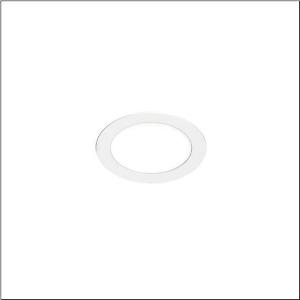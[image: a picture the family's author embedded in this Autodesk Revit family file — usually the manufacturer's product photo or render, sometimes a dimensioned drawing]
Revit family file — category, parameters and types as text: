
# Revit family: lunis_41_flat_51dr107dhba
name_source: partatom
category: Lighting Fixtures
units: mm (PartAtom-declared; Revit-internal decimal feet)

## family parameters
Cut with Voids When Loaded = No
Host = Face
Light Source = No
Part Type = Normal
Room Calculation Point = No
Round Connector Dimension = Use Diameter
Shared = No

## types (1)
- --- (1 x LED, 1360 lm, 15 W, 5700K)
    Apparent Load = 15 VA
    CIE Flux Codes = 49 80 96 100 100
    Color Rendering = 80
    Color Temperature = 5700K
    Default Elevation = 1800 mm
    Description = Lunis 41,  flat, downlight, light emission: direct distribution, LED rated luminous flux: 1.360lm, light colour: 840/857, control gear: ECG, mains connection: 230V, AC, 50/60Hz, housing, round, of aluminium, coated, traffic white (RAL 9016), diameter: 170mm, protection rating (complete): IP20, protection rating (on room side): IP44, insulation class (complete): insulation class II (safety insulation), certification: CE, permissible ambient temperature for indoor applications: -20..+40°C, packaging unit: 1 piece
    Height = 0 mm  [stored 0 ft]
    Lamp = 1 x LED
    Lamp Light Flux = 1360 lm
    Lamp Power = 15 W
    Lamp count = 1
    Length = 170 mm  [stored 0.557743 ft]
    Luminous efficacy = 91 lm/W
    Manufacturer = Siteco
    ModVariant = No
    Model = 51DR107DHBA
    Mounting Place = Ceiling
    Mounting Type = Recessed
    Number of Poles = 1
    OnlyDefault = Yes
    Power Factor = 1
    Product Name = Lunis 41 flat
    Product group = downlight
    ProductGroupID = 400
    Protection Class = Protection class II
    Protection Degree = IP 20
    RLX_Detail_Level = 1
    RLX_Emergency_Light_Flux = 0 lm
    RLX_Emergency_Type = 0
    RLX_Emergency_Type_DB = No
    RlxData = <blob elided: 24273 chars, md5=9e7785de>
    Socket = socket
    Standby Power = 0 W
    System Light Flux = 1360 lm
    System Power = 15 W
    Type Comments = factory setting: colour temperature 5700K
    Type Image = l_1007045.jpg
    URL = http://relux.com
    VarID = @adj_130679
    Voltage = 0 V
    Weight = 0.00 kg
    Width = 0 mm  [stored 0 ft]

note: [stored X ft] marks values corroborated as IEEE doubles in the binary element streams (Revit-internal decimal feet)

## geometry (parser evidence)
native form markers: Blend x4, Sweep x10
no freeform markers — native parametric forms only
